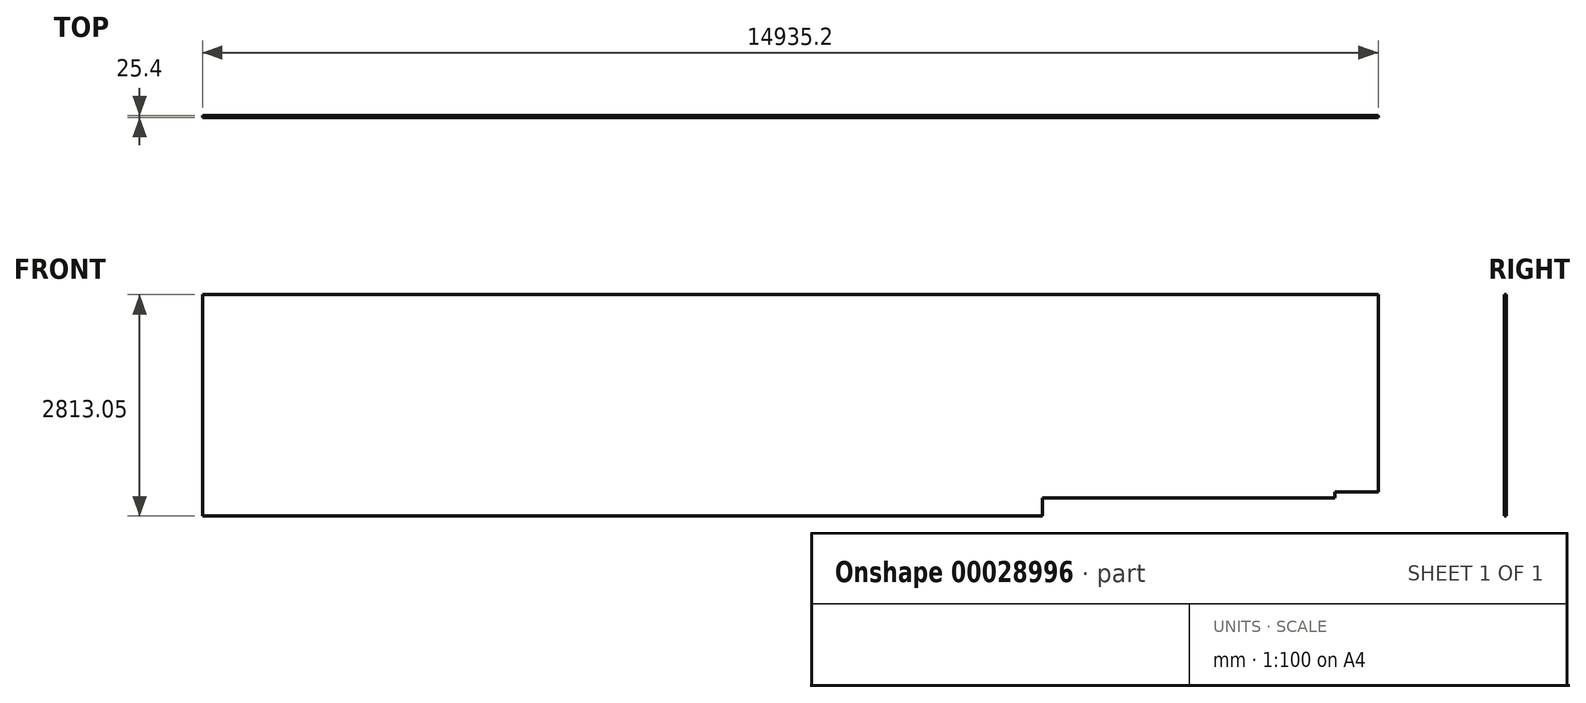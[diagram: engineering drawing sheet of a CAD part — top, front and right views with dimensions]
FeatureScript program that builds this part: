
annotation { "Feature Type Name" : "Feature", "Feature Type Description" : "" }
export const myFeature = defineFeature(function(context is Context, id is Id, definition is map)
    precondition{}
    {
        {
            var Q0;
            Q0=qCreatedBy(makeId("Front.planeOp"),FACE);
            var sketch = newSketch(context, id + "F0", { "sketchPlane" : qUnion([Q0])});
            skLineSegment(sketch, "E0", {"start": v(0, 2755.9) * mm, "end": v(14935.2, 2755.9) * mm});
            skLineSegment(sketch, "E1", {"start": v(14554.2, 2813.05) * mm, "end": v(14554.2, 361.95) * mm});
            skLineSegment(sketch, "E2", {"start": v(14554.2, 361.95) * mm, "end": v(14325.6, 361.95) * mm});
            skLineSegment(sketch, "E3", {"start": v(14325.6, 361.95) * mm, "end": v(14325.6, 285.75) * mm});
            skLineSegment(sketch, "E4", {"start": v(14325.6, 285.75) * mm, "end": v(10668, 285.75) * mm});
            skLineSegment(sketch, "E5", {"start": v(10668, 285.75) * mm, "end": v(10668, 57.15) * mm});
            skLineSegment(sketch, "E6", {"start": v(10668, 57.15) * mm, "end": v(0, 57.15) * mm});
            skLineSegment(sketch, "E7", {"start": v(304.8, 0) * mm, "end": v(304.8, 2813.05) * mm});
            skPoint(sketch, "E8.orphan", {"position": v(304.8, 57.15) * mm});
            skLineSegment(sketch, "E9.0", {"start": v(0, 2698.75) * mm, "end": v(14935.2, 2698.75) * mm, "construction": true});
            skLineSegment(sketch, "E10.0", {"start": v(381, 2813.05) * mm, "end": v(14376.4, 2813.05) * mm});
            skLineSegment(sketch, "E11.0", {"start": v(10668, 0) * mm, "end": v(374.65, 0) * mm});
            skLineSegment(sketch, "E12.0", {"start": v(10668, 114.3) * mm, "end": v(0, 114.3) * mm, "construction": true});
            skLineSegment(sketch, "E13.0", {"start": v(0, 82.55) * mm, "end": v(0, 2667) * mm});
            skLineSegment(sketch, "E14.0", {"start": v(609.6, 57.15) * mm, "end": v(609.6, 2813.05) * mm, "construction": true});
            skPoint(sketch, "E15.orphan", {"position": v(304.8, 2616.2) * mm});
            skLineSegment(sketch, "E16.0", {"start": v(14935.2, 2667) * mm, "end": v(14935.2, 304.8) * mm});
            skLineSegment(sketch, "E17.0", {"start": v(14935.2, 419.1) * mm, "end": v(14268.45, 419.1) * mm, "construction": true});
            skLineSegment(sketch, "E18.0", {"start": v(14935.2, 304.8) * mm, "end": v(14382.75, 304.8) * mm});
            skLineSegment(sketch, "E19.0", {"start": v(14268.45, 419.1) * mm, "end": v(14268.45, 285.75) * mm, "construction": true});
            skLineSegment(sketch, "E20.0", {"start": v(14382.75, 304.8) * mm, "end": v(14382.75, 228.6) * mm});
            skLineSegment(sketch, "E21.0", {"start": v(14325.6, 342.9) * mm, "end": v(10668, 342.9) * mm, "construction": true});
            skLineSegment(sketch, "E22.0", {"start": v(14382.75, 228.6) * mm, "end": v(10668, 228.6) * mm});
            skLineSegment(sketch, "E23", {"start": v(14382.75, 304.8) * mm, "end": v(14325.6, 361.95) * mm});
            skLineSegment(sketch, "E24", {"start": v(14173.2, 423.8) * mm, "end": v(14173.2, 2813.05) * mm, "construction": true});
            skLineSegment(sketch, "E25", {"start": v(10668, 0) * mm, "end": v(10668, 57.15) * mm});
            skLineSegment(sketch, "E26", {"start": v(0, 2667) * mm, "end": v(0, 2813.05) * mm});
            skLineSegment(sketch, "E27", {"start": v(0, 2813.05) * mm, "end": v(381, 2813.05) * mm});
            skLineSegment(sketch, "E28", {"start": v(0, 82.55) * mm, "end": v(0, 0) * mm});
            skLineSegment(sketch, "E29", {"start": v(0, 0) * mm, "end": v(374.65, 0) * mm});
            skLineSegment(sketch, "E30", {"start": v(14376.4, 2813.05) * mm, "end": v(14935.2, 2813.05) * mm});
            skLineSegment(sketch, "E31", {"start": v(14935.2, 2813.05) * mm, "end": v(14935.2, 2667) * mm});
            skSolve(sketch);
        }
        {
            var Q0;
            Q0 = qSketchRegion(id + "F0", true);
            extrude(context, id + "F1", {"entities" : qUnion([Q0]), "depth" : 25.4 * mm});
        }
    });
